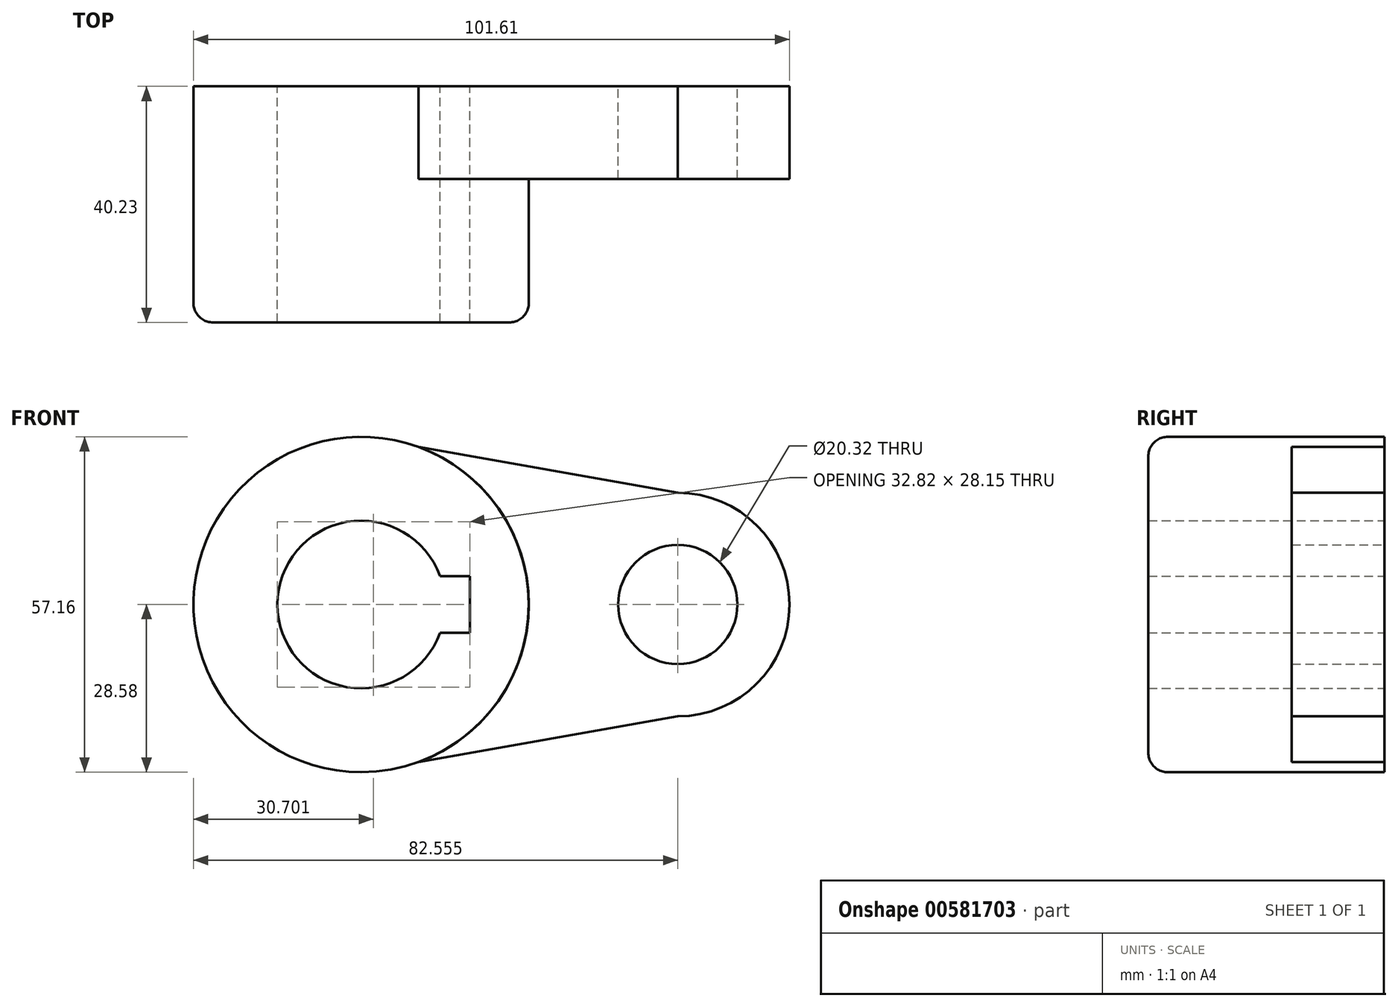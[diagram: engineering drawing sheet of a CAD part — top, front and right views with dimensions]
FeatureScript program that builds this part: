
annotation { "Feature Type Name" : "Feature", "Feature Type Description" : "" }
export const myFeature = defineFeature(function(context is Context, id is Id, definition is map)
    precondition{}
    {
        {
            var Q0;
            Q0=qCreatedBy(makeId("Front.planeOp"),FACE);
            var sketch = newSketch(context, id + "F0", { "sketchPlane" : qUnion([Q0])});
            skCircle(sketch, "E0", {"center": v(0, 0) * mm, "radius": 28.58 * mm});
            skPoint(sketch, "E1", {"position": v(53.98, 0) * mm});
            skCircle(sketch, "E2", {"center": v(53.98, 0) * mm, "radius": 10.16 * mm});
            skArc(sketch, "E3", {"start": v(13.45, 4.83) * mm, "mid": v(-14.29, 0) * mm, "end": v(13.45, -4.83) * mm});
            skLineSegment(sketch, "E4.bottom", {"start": v(13.45, 4.83) * mm, "end": v(18.53, 4.83) * mm});
            skLineSegment(sketch, "E4.top", {"start": v(13.45, -4.83) * mm, "end": v(18.53, -4.83) * mm});
            skLineSegment(sketch, "E4.right", {"start": v(18.53, 4.83) * mm, "end": v(18.53, -4.83) * mm});
            skPoint(sketch, "E5.orphan", {"position": v(-18.53, 4.83) * mm});
            skPoint(sketch, "E6.orphan", {"position": v(-18.53, -4.83) * mm});
            skArc(sketch, "E7", {"start": v(53.97, -19.05) * mm, "mid": v(73.03, 0) * mm, "end": v(53.98, 19.05) * mm});
            skPoint(sketch, "E8", {"position": v(53.98, 19.05) * mm});
            skPoint(sketch, "E9", {"position": v(53.98, -19.05) * mm});
            skPoint(sketch, "E10", {"position": v(0, 28.58) * mm});
            skFitSpline(sketch, "E11", {"points": [v(53.98, 19.05) * mm, v(0, 28.58) * mm], "startDerivative": vector(-53.98, 9.53) * mm, "endDerivative": vector(-53.98, 9.53) * mm});
            skFitSpline(sketch, "E12", {"points": [v(53.98, -19.05) * mm, v(0, -28.58) * mm], "startDerivative": vector(-53.98, -9.53) * mm, "endDerivative": vector(-53.98, -9.53) * mm});
            skSolve(sketch);
        }
        {
            var Q0;
            Q0=makeQuery(id+"F0.imprint","IMPRINT",FACE,{"disambiguationData":[TD([[makeQuery(id+"F0.imprint","IMPRINT",EDGE,{"derivedFrom":sQuery(id+"F0.wireOp",EDGE,"E0")}),1.0]])]});
            extrude(context, id + "F1", {"entities" : qUnion([Q0]), "depth" : 40.23 * mm, "offsetDistance" : 25.4 * mm});
        }
        {
            var Q0;
            Q0 = qSketchRegion(id + "F0", true);
            extrude(context, id + "F2", {"entities" : qUnion([Q0]), "operationType" : NewBodyOperationType.ADD, "depth" : 15.77 * mm, "offsetDistance" : 25.4 * mm});
        }
        {
            var Q0;
            Q0=makeQuery(id+"F1.opExtrude","CAP_EDGE",EDGE,{"disambiguationData":[OSD([sQuery(id+"F0.wireOp",EDGE,"E0")])],"isStart":false});
            fillet(context, id + "F3", {"entities" : qUnion([Q0]), "radius" : 3.3 * mm, "tangentPropagation" : true, "allowEdgeOverflow" : false});
        }
    });
